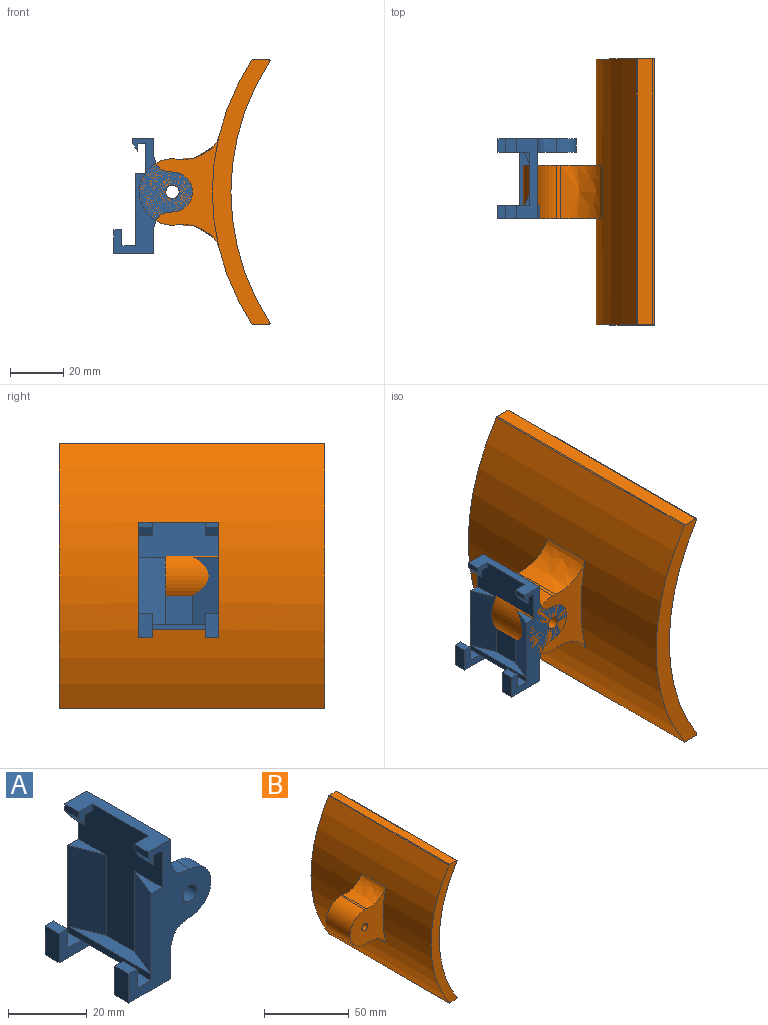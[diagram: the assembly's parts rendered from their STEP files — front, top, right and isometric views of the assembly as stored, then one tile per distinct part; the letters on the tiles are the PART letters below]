
ASSEMBLY  parts=2 mates=1
PART A: 60 faces, bbox 30.3x30.8x44.2 mm
  f0: plane 44.19x30.29mm, normal (0,1,0), area 373.4mm2, adj f3,f8,f9,f10,f11,f13,f16,f17
  f1: plane 5x3mm, normal (1,0,0), area 15mm2, adj f2,f5,f6,f7
  f2: plane 5x3mm, normal (0,0,-1), area 15mm2, adj f1,f6,f7,f13
  f3: plane 30x8mm, normal (0,0,1), area 140mm2, adj f0,f4,f6,f7,f10,f12,f13,f17
  f4: plane 5x2mm, normal (-1,0,0), area 10mm2, adj f3,f5,f6,f7
  f5: plane 5x3mm, normal (-0.83,0,-0.55), area 18mm2, adj f1,f4,f6,f7
  f6: plane 5x5mm, normal (0,1,0), area 13mm2, adj f1,f2,f3,f4,f5,f13
  f7: plane 43.4x29.5mm, normal (0,-1,0), area 497mm2, adj f1,f2,f3,f4,f5,f13,f15,f16
  f8: plane 5x3mm, normal (1,0,0), area 15mm2, adj f0,f9,f11,f12
  f9: plane 5x3mm, normal (0,0,-1), area 15mm2, adj f0,f8,f12,f13
  f10: plane 5x2mm, normal (-1,0,0), area 10mm2, adj f0,f3,f11,f12
  f11: plane 5x3mm, normal (-0.83,0,-0.55), area 18mm2, adj f0,f8,f10,f12
  f12: plane 5x5mm, normal (0,-1,0), area 13mm2, adj f3,f8,f9,f10,f11,f13
  f13: plane 38.4x30mm, normal (-1,0,0), area 632mm2, adj f0,f2,f3,f6,f7,f9,f12,f15
  f14: plane 20x7mm, normal (0,0,-1), area 140mm2, adj f16,f17,f27,f33
  f15: plane 10x4mm, normal (0,0,1), area 20mm2, adj f7,f13,f19
  f16: plane 30x2mm, normal (-1,0,0), area 60mm2, adj f0,f7,f14,f21,f22,f28
  f17: plane 43.4x30mm, normal (1,0,0), area 975.9mm2, adj f0,f3,f7,f14,f26,f27,f32,f33
  f18: plane 10x4mm, normal (0,0,1), area 20mm2, adj f0,f13,f20
  f19: plane 25x10mm, normal (-0.93,0.37,0), area 269.3mm2, adj f7,f13,f15,f21
  f20: plane 25x10mm, normal (-0.93,-0.37,0), area 269.3mm2, adj f0,f13,f18,f21
  f21: plane 30x4mm, normal (0,0,1), area 80mm2, adj f13,f16,f19,f20
  f22: plane 5x5mm, normal (0,0,1), area 25mm2, adj f7,f16,f23,f27
  f23: plane 6x5mm, normal (1,0,0), area 30mm2, adj f7,f22,f24,f27
  f24: plane 5x3mm, normal (0,0,1), area 15mm2, adj f7,f23,f25,f27
  f25: plane 9x5mm, normal (-1,0,0), area 45mm2, adj f7,f24,f26,f27
  f26: plane 15x5mm, normal (0,0,-1), area 75mm2, adj f7,f17,f25,f27
  f27: plane 15x9mm, normal (0,1,0), area 63mm2, adj f14,f17,f22,f23,f24,f25,f26
  f28: plane 5x5mm, normal (0,0,1), area 25mm2, adj f0,f16,f29,f33
  f29: plane 6x5mm, normal (1,0,0), area 30mm2, adj f0,f28,f30,f33
  f30: plane 5x3mm, normal (0,0,1), area 15mm2, adj f0,f29,f31,f33
  f31: plane 9x5mm, normal (-1,0,0), area 45mm2, adj f0,f30,f32,f33
  f32: plane 15x5mm, normal (0,0,-1), area 75mm2, adj f0,f17,f31,f33
  f33: plane 15x9mm, normal (0,-1,0), area 63mm2, adj f14,f17,f28,f29,f30,f31,f32
  f34: extruded ~7x5.81mm, area 50.3mm2, adj f7,f17,f35,f38
  f35: cylinder r=7.5mm len=15mm, axis (0,-1,0), area 117.8mm2, adj f7,f34,f36,f38
  f36: extruded ~7x5.81mm, area 50.3mm2, adj f7,f17,f35,f38
  f37: cylinder r=2.5mm len=5mm, axis (0,-1,0), area 78.5mm2, adj f7,f38
  f38: plane 26.61x14.5mm, normal (0,1,0), area 191.8mm2, adj f17,f34,f35,f36,f37
  f39: extruded ~7x5.81mm, area 50.3mm2, adj f0,f17,f40,f43
  f40: cylinder r=7.5mm len=15mm, axis (0,1,0), area 117.8mm2, adj f0,f39,f41,f43
  f41: extruded ~7x5.81mm, area 50.3mm2, adj f0,f17,f40,f43
  f42: cylinder r=2.5mm len=5mm, axis (0,1,0), area 78.5mm2, adj f0,f43
  f43: plane 26.82x14.6mm, normal (0,-1,0), area 191.8mm2, adj f17,f39,f40,f41,f42
  f44: plane 21.9x10.16mm, normal (0,1,0), area 78.4mm2, adj f45,f46,f47,f51,f53,f54
  f45: cylinder r=5mm len=10mm, axis (0,1,0), area 38.6mm2, adj f0,f44,f46,f47
  f46: extruded ~7.37x3.18mm, area 20.8mm2, adj f0,f44,f45,f53
  f47: extruded ~9.37x7.93mm, area 33.7mm2, adj f0,f44,f45,f54
  f48: plane 3x0.81mm, normal (0,1,0), area 2.4mm2, adj f49,f50,f52,f54
  f49: plane 2.5x1.81mm, normal (0,0,1), area 3.3mm2, adj f0,f48,f50,f54
  f50: plane 25x4.52mm, normal (0.93,0.37,0), area 115.1mm2, adj f0,f48,f49,f51,f52,f54
  f51: plane 4.52x3.81mm, normal (0,0,-1), area 9.1mm2, adj f0,f44,f50,f53,f54
  f52: plane 2.02x0.81mm, normal (0,0,1), area 0.8mm2, adj f48,f50,f54
  f53: plane 3.88x2.5mm, normal (1,0,0), area 9.7mm2, adj f0,f44,f46,f51
  f54: plane 25x4.52mm, normal (-1,0,0), area 63.8mm2, adj f0,f44,f47,f48,f49,f50,f51,f52
  f55: plane 22x2.02mm, normal (0.93,-0.37,0), area 47.8mm2, adj f56,f57,f58,f59
  f56: plane 2.02x0.81mm, normal (0,0,-1), area 0.8mm2, adj f55,f58,f59
  f57: plane 2.02x0.81mm, normal (0,0,1), area 0.8mm2, adj f55,f58,f59
  f58: plane 22x2.02mm, normal (-1,0,0), area 44.4mm2, adj f55,f56,f57,f59
  f59: plane 22x0.81mm, normal (0,1,0), area 17.8mm2, adj f55,f56,f57,f58
PART B: 18 faces, bbox 49.2x100x100 mm
  f0: extruded ~20x1.43mm, area 28.6mm2, adj f1,f4,f6,f7
  f1: cylinder r=12.5mm len=25mm, axis (0,1,0), area 785.4mm2, adj f0,f2,f6,f7
  f2: extruded ~20x1.43mm, area 28.6mm2, adj f1,f3,f6,f7
  f3: extruded ~20x15.85mm, area 376.8mm2, adj f2,f6,f7,f8
  f4: extruded ~20x15.85mm, area 376.8mm2, adj f0,f6,f7,f8
  f5: cylinder r=2.5mm len=20mm, axis (0,1,0), area 314.2mm2, adj f6,f7
  f6: plane 40.24x29.77mm, normal (0,-1,0), area 647.7mm2, adj f0,f1,f2,f3,f4,f5,f8
  f7: plane 40.24x29.77mm, normal (0,1,0), area 647.7mm2, adj f0,f1,f2,f3,f4,f5,f8
  f8: cylinder r=90.14mm len=100mm, axis (0,1,0), area 9734.9mm2, adj f3,f4,f6,f7,f9,f15,f16,f17
  f9: cylinder r=0.5mm len=100mm, axis (0,1,0), area 49.3mm2, adj f8,f10,f16,f17
  f10: plane 100x5.8mm, normal (0,0,-1), area 580.3mm2, adj f9,f11,f16,f17
  f11: cylinder r=0.5mm len=100mm, axis (0,1,0), area 107.4mm2, adj f10,f12,f16,f17
  f12: cylinder r=90.14mm len=100mm, axis (0,1,0), area 10415.2mm2, adj f11,f13,f16,f17
  f13: cylinder r=0.5mm len=100mm, axis (0,1,0), area 107.4mm2, adj f12,f14,f16,f17
  f14: plane 100x5.8mm, normal (0,0,1), area 580.3mm2, adj f13,f15,f16,f17
  f15: cylinder r=0.5mm len=100mm, axis (0,1,0), area 49.3mm2, adj f8,f14,f16,f17
  f16: plane 100x21.71mm, normal (0,-1,0), area 699.6mm2, adj f8,f9,f10,f11,f12,f13,f14,f15
  f17: plane 100x21.71mm, normal (0,1,0), area 699.6mm2, adj f8,f9,f10,f11,f12,f13,f14,f15
PLACE A at identity
PLACE B t=(47.14,-5,0)mm
MATE cylindrical B.f1 <-> A.f37  axis (0,-1,0) through (10,-15,0)mm
